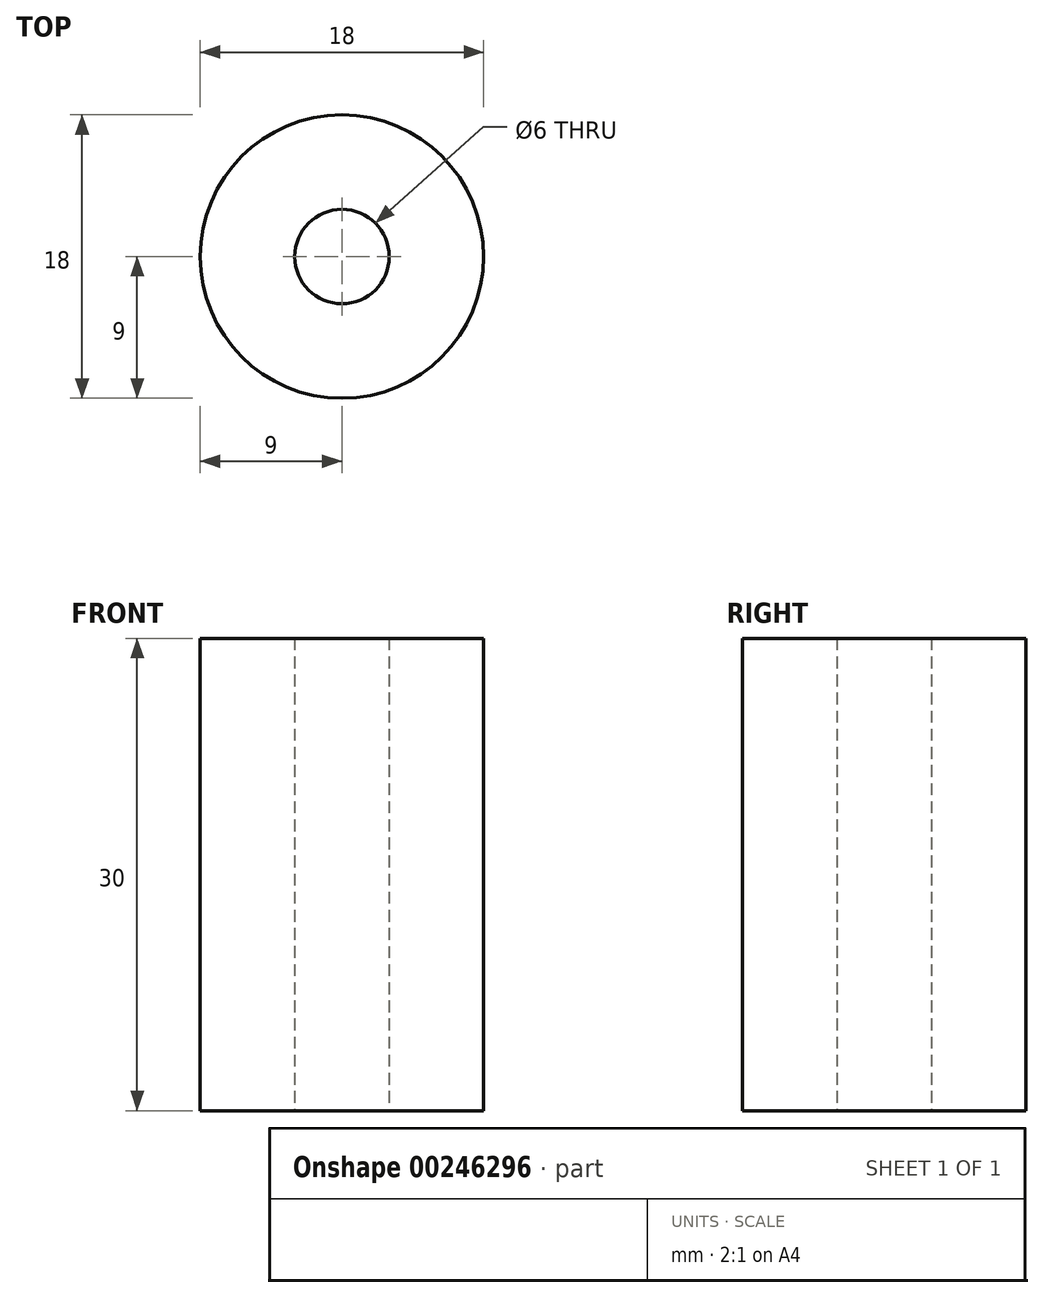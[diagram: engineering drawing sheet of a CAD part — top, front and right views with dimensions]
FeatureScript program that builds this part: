
annotation { "Feature Type Name" : "Feature", "Feature Type Description" : "" }
export const myFeature = defineFeature(function(context is Context, id is Id, definition is map)
    precondition{}
    {
        {
            var Q0;
            Q0=qCreatedBy(makeId("Top.planeOp"),FACE);
            var sketch = newSketch(context, id + "F0", { "sketchPlane" : qUnion([Q0])});
            skCircle(sketch, "E0", {"center": v(0, 0) * mm, "radius": 3 * mm});
            skCircle(sketch, "E1", {"center": v(0, 0) * mm, "radius": 9 * mm});
            skSolve(sketch);
        }
        {
            var Q0;
            Q0 = qSketchRegion(id + "F0", true);
            extrude(context, id + "F1", {"entities" : qUnion([Q0]), "depth" : 30 * mm});
        }
    });
